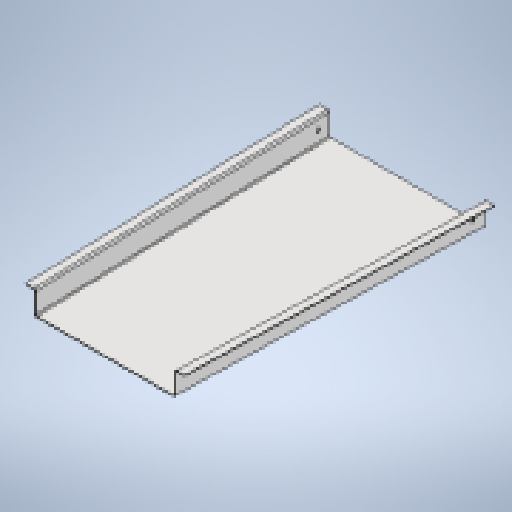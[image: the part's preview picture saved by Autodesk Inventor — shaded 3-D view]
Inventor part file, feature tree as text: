
AUTODESK INVENTOR PART (.ipt)
format: ipt  version: 2025.1 (Build 291241020, 241B)  size: 236,544 bytes
history: native  units: mm
features: sheet_metal_op x4, other x4, sketch x3, extrude x1, projected_geometry x1
ambient origin geometry x8: Origin, YZ Plane, XZ Plane, XY Plane, X Axis, Y Axis, Z Axis, Center Point
bodies: Solid1 (feature_tree)
feature tree (13):
  sheet_metal_op  "Face1"
  other  "A-Side Definition"
  sheet_metal_op  "Flange1"
  extrude  "Extrusion1"  Depth=2.0mm
  sketch  "Sketch1"  dims[d0=460.0mm d2=2.0mm]
  other  "Plate1"
  sketch  "Sketch3"  dims[d12=2.0mm]
  other  "Plate2"
  sheet_metal_op  "Bend1"
  sheet_metal_op  "Corner1"
  sketch  "Sketch5"  dims[d13=1.0mm d14=4.0mm d15=2.75mm d16=60.0mm d17=90.0deg d18=2.75mm d19=8.0mm d20=2.0mm d21=2.75mm d23=350.0mm d24=40.0mm d25=480.225352mm d26=1300.0mm d27=750.0mm d38=396.0mm d39=10.0mm d40=30.0mm d42=0.0mm d43=0.0mm]
  projected_geometry  "Projected Loop1"
  other  "Definition1"
